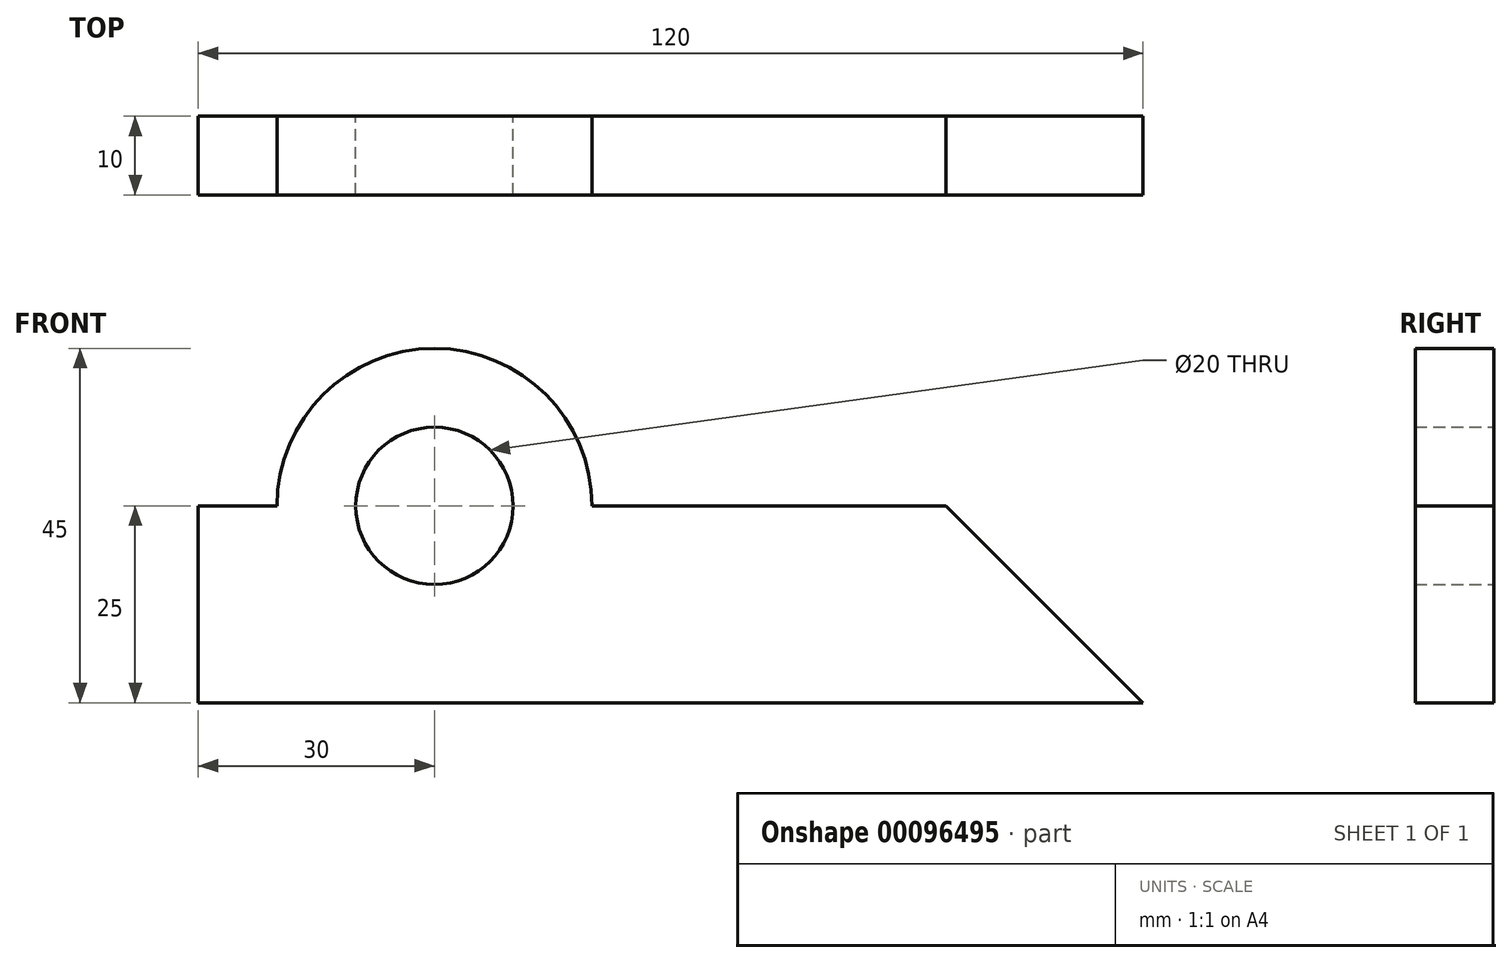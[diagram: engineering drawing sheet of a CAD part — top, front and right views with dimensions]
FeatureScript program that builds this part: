
annotation { "Feature Type Name" : "Feature", "Feature Type Description" : "" }
export const myFeature = defineFeature(function(context is Context, id is Id, definition is map)
    precondition{}
    {
        {
            var Q0;
            Q0=qCreatedBy(makeId("Front.planeOp"),FACE);
            var sketch = newSketch(context, id + "F0", { "sketchPlane" : qUnion([Q0])});
            skLineSegment(sketch, "E0", {"start": v(0, 0) * mm, "end": v(120, 0) * mm});
            skLineSegment(sketch, "E1", {"start": v(120, 0) * mm, "end": v(95, 25) * mm});
            skLineSegment(sketch, "E2", {"start": v(0, 25) * mm, "end": v(0, 0) * mm});
            skArc(sketch, "E3", {"start": v(10, 25) * mm, "mid": v(30, 45) * mm, "end": v(50, 25) * mm});
            skCircle(sketch, "E4", {"center": v(30, 25) * mm, "radius": 10 * mm});
            skLineSegment(sketch, "E5", {"start": v(0, 25) * mm, "end": v(10, 25) * mm});
            skLineSegment(sketch, "E6", {"start": v(50, 25) * mm, "end": v(95, 25) * mm});
            skSolve(sketch);
        }
        {
            var Q0;
            Q0=makeQuery(id+"F0.imprint","IMPRINT",FACE,{"disambiguationData":[TD([[makeQuery(id+"F0.imprint","IMPRINT",EDGE,{"derivedFrom":sQuery(id+"F0.wireOp",EDGE,"E0")}),1.0]])]});
            extrude(context, id + "F1", {"entities" : qUnion([Q0]), "depth" : 10 * mm});
        }
    });
